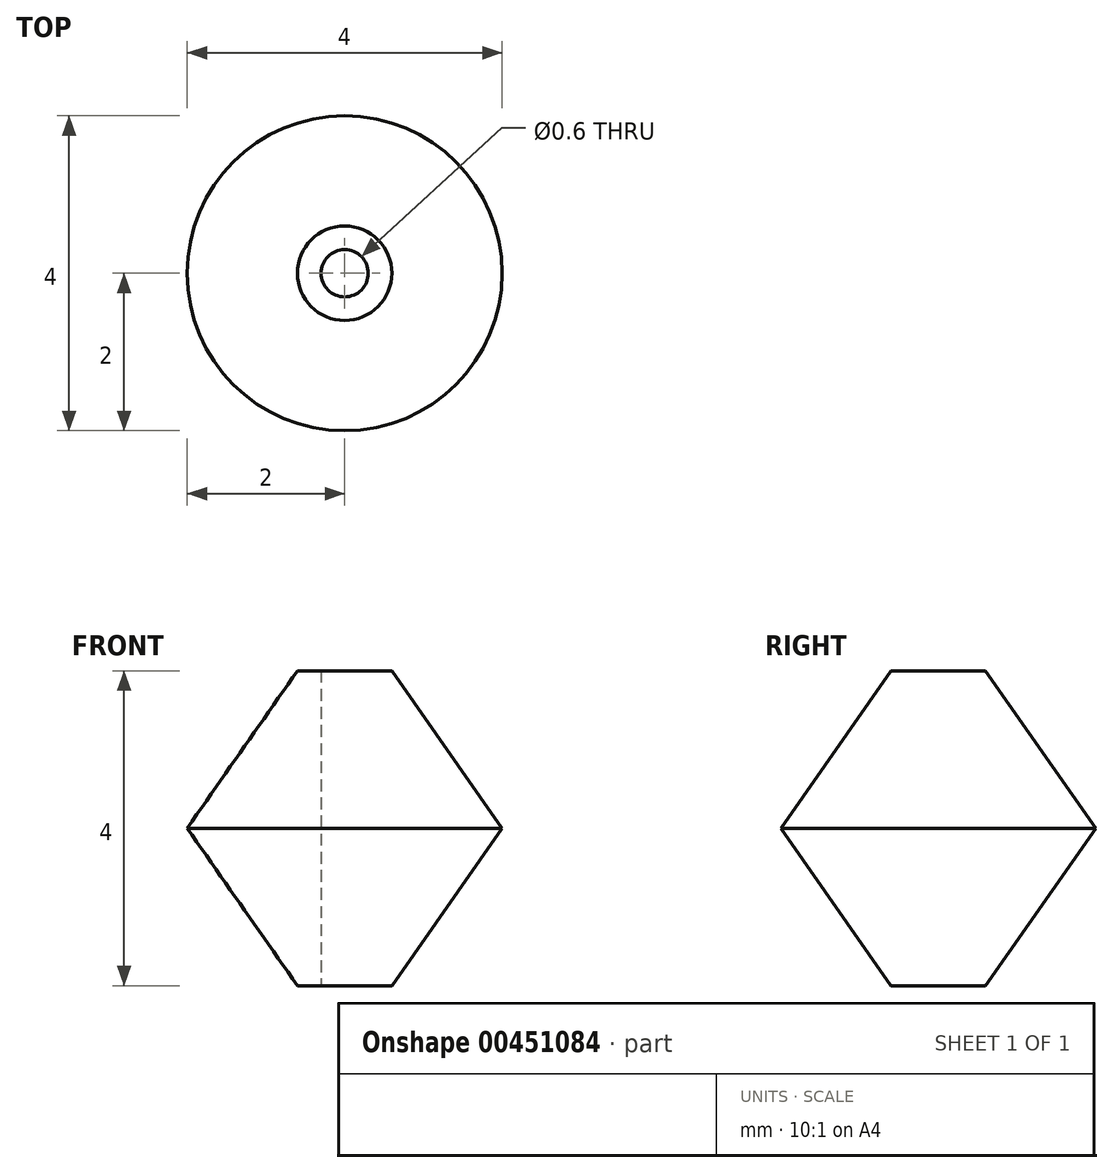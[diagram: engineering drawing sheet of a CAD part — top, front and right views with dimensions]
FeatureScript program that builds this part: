
annotation { "Feature Type Name" : "Feature", "Feature Type Description" : "" }
export const myFeature = defineFeature(function(context is Context, id is Id, definition is map)
    precondition{}
    {
        {
            var Q0;
            Q0=qCreatedBy(makeId("Front.planeOp"),FACE);
            var sketch = newSketch(context, id + "F0", { "sketchPlane" : qUnion([Q0])});
            skLineSegment(sketch, "E0.bottom", {"start": v(0, 0) * mm, "end": v(0.3, 0) * mm});
            skLineSegment(sketch, "E0.top", {"start": v(0, 2) * mm, "end": v(0.3, 2) * mm});
            skLineSegment(sketch, "E0.left", {"start": v(0, 0) * mm, "end": v(0, 2) * mm});
            skLineSegment(sketch, "E0.right", {"start": v(0.3, 0) * mm, "end": v(0.3, 2) * mm});
            skLineSegment(sketch, "E1.bottom", {"start": v(0.3, 2) * mm, "end": v(0.6, 2) * mm});
            skLineSegment(sketch, "E1.top", {"start": v(0.3, 0) * mm, "end": v(0.6, 0) * mm});
            skLineSegment(sketch, "E1.left", {"start": v(0.3, 2) * mm, "end": v(0.3, 0) * mm});
            skLineSegment(sketch, "E1.right", {"start": v(0.6, 2) * mm, "end": v(0.6, 0) * mm});
            skLineSegment(sketch, "E2", {"start": v(0.6, 0) * mm, "end": v(2, 0) * mm});
            skLineSegment(sketch, "E3", {"start": v(0.6, 2) * mm, "end": v(2, 0) * mm});
            skLineSegment(sketch, "E4.MirrorCS", {"start": v(0.6, -2) * mm, "end": v(2, 0) * mm});
            skLineSegment(sketch, "E5.MirrorCS", {"start": v(0.3, -2) * mm, "end": v(0.6, -2) * mm});
            skLineSegment(sketch, "E6.MirrorCS", {"start": v(0.3, -2) * mm, "end": v(0.3, 0) * mm});
            skSolve(sketch);
        }
        {
            var Q0;
            Q0=makeQuery(id+"F0.imprint","IMPRINT",FACE,{"disambiguationData":[TD([[makeQuery(id+"F0.imprint","IMPRINT",EDGE,{"derivedFrom":sQuery(id+"F0.wireOp",EDGE,"E1.top")}),-1.0]])]});
            var Q1;
            Q1=makeQuery(id+"F0.imprint","IMPRINT",FACE,{"disambiguationData":[TD([[makeQuery(id+"F0.imprint","IMPRINT",EDGE,{"derivedFrom":sQuery(id+"F0.wireOp",EDGE,"E1.right")}),1.0]])]});
            var Q2;
            Q2=makeQuery(id+"F0.imprint","IMPRINT",FACE,{"disambiguationData":[TD([[makeQuery(id+"F0.imprint","IMPRINT",EDGE,{"derivedFrom":sQuery(id+"F0.wireOp",EDGE,"E1.bottom")}),-1.0]])]});
            var Q3;
            Q3=sQuery(id+"F0.wireOp",EDGE,"E0.left");
            revolve(context, id + "F1", {"entities" : qUnion([Q0, Q1, Q2]), "axis" : qUnion([Q3]), "revolveType" : RevolveType.FULL});
        }
    });
